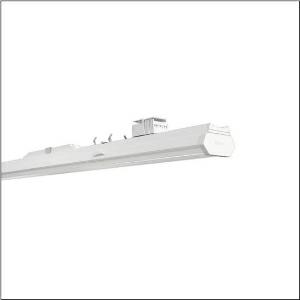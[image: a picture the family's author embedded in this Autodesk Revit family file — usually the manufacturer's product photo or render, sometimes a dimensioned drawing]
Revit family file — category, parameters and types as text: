
# Revit family: licross_r__11_protected_ho_51td13cn4e5s_07e4
name_source: partatom
category: Lighting Fixtures
units: mm (PartAtom-declared; Revit-internal decimal feet)

## family parameters
Cut with Voids When Loaded = No
Host = Face
Light Source = No
Part Type = Normal
Room Calculation Point = No
Round Connector Dimension = Use Diameter
Shared = No

## types (1)
- --- (1 x LED, 14500 lm, 77.6 W, 4000K)
    Apparent Load = 78 VA
    CIE Flux Codes = 89 96 99 100 99
    Color Rendering = 80
    Color Temperature = 4000K
    Default Elevation = 1800 mm
    Description = Licross® 11 Protected HO, luminaire insert, of sheet steel, galvanised, coil coated, white, length: 1.500mm, width: 90mm, height: 101mm, LED rated luminous flux: 14.500lm, light colour: 840, control gear: ON/OFF Multilumen, CLOi, with plug, 3-pole, with phase selection, mains connection: 220..240V, AC, 50/60Hz, start of lifetime: 78W, end of service life: 87W, halogen-free wiring, primary light control with lens, of plastic, primary optical cover: cover, of PMMA, light emission: direct distribution, primary light characteristic: symmetric, protection rating (complete): IP54, insulation class (complete): insulation class I (protective earthing), certification: CE, ENEC, VDE, UKCA, protection symbol: D if used in an environment with non-conductive dust loads with corresponding accessories, impact resistance: IK06, permissible ambient temperature for indoor applications: -35..+35°C, corresponds to IFS (International Featured Standards) requirements for safety and quality in the food industry, reducing of maximum allowable ambient temperature of 5°C with ceiling mounting, LABS conformity tested according to VDMA 24364:2018-05, packaging unit: 1 piece
    Height = 92 mm
    Lamp = 1 x LED
    Lamp Light Flux = 14500 lm
    Lamp Power = 77.6 W
    Lamp count = 1
    Length = 1500 mm
    Luminous efficacy = 187 lm/W
    Manufacturer = Siteco
    ModVariant = No
    Model = 51TD13CN4E5S
    Mounting Place = Ceiling
    Mounting Type = Pendant
    Number of Poles = 1
    OnlyDefault = Yes
    Power Factor = 1
    Product Name = Licross® 11 Protected HO
    Product group = luminaire insert
    ProductGroupID = 902
    Protection Class = Protection class I
    Protection Degree = IP 54
    RLX_Detail_Level = 1
    RLX_Emergency_Light_Flux = 0 lm
    RLX_Emergency_Type = 0
    RLX_Emergency_Type_DB = No
    RlxData = <blob elided: 22085 chars, md5=2422b864>
    Socket = socket
    Standby Power = 0 W
    System Light Flux = 14500 lm
    System Power = 78 W
    Type Comments = factory setting: luminous flux: 100 % | (A | C | E) | 181 mA
    Type Image = l_1256145.jpg
    URL = http://relux.com
    VarID = @adj_085692
    Voltage = 0 V
    Weight = 0.00 kg
    Width = 88 mm

## geometry (parser evidence)
native form markers: Blend x4, Sweep x10
no freeform markers — native parametric forms only
